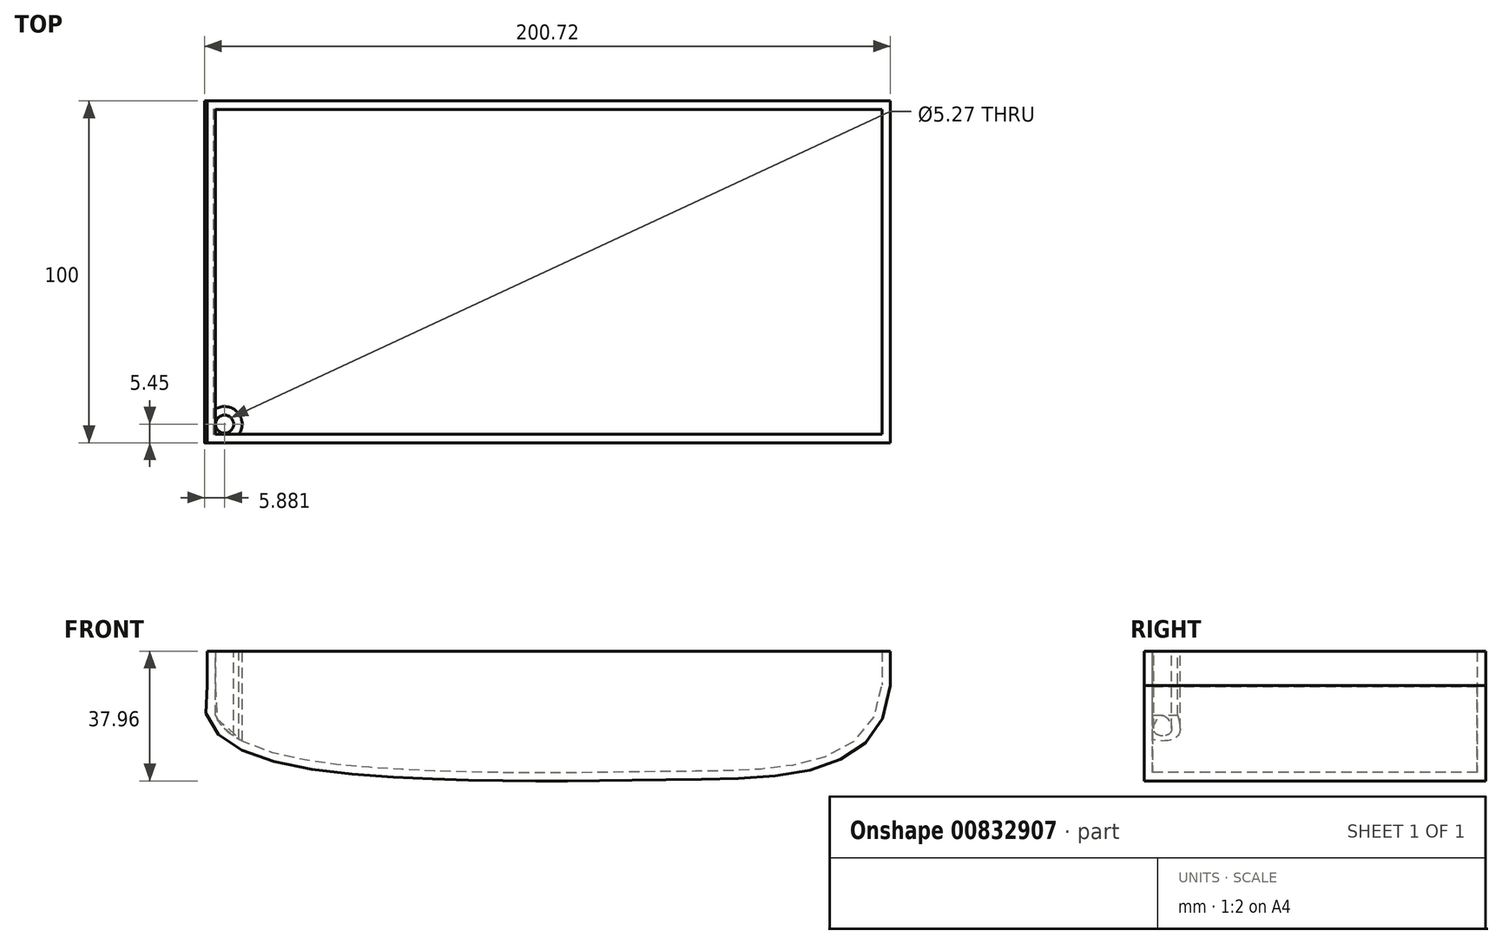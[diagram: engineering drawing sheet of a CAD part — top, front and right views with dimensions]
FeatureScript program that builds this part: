
annotation { "Feature Type Name" : "Feature", "Feature Type Description" : "" }
export const myFeature = defineFeature(function(context is Context, id is Id, definition is map)
    precondition{}
    {
        {
            var Q0;
            Q0=qCreatedBy(makeId("Front.planeOp"),FACE);
            var sketch = newSketch(context, id + "F0", { "sketchPlane" : qUnion([Q0])});
            skLineSegment(sketch, "E0.bottom", {"start": v(-100.49, -20.47) * mm, "end": v(99.51, -20.47) * mm});
            skLineSegment(sketch, "E0.left", {"start": v(-100.49, -20.47) * mm, "end": v(-100.49, -30.47) * mm});
            skLineSegment(sketch, "E0.right", {"start": v(99.51, -20.47) * mm, "end": v(99.51, -30.47) * mm});
            skFitSpline(sketch, "E1", {"points": [v(-100.49, -30.47) * mm, v(-42.17, -57.48) * mm, v(39.99, -57.98) * mm, v(99.51, -30.47) * mm], "startDerivative": vector(-59.48, -210.03) * mm, "endDerivative": vector(16.46, 256.73) * mm});
            skPoint(sketch, "E2.orphan", {"position": v(-100.49, -45.47) * mm});
            skPoint(sketch, "E3.orphan", {"position": v(99.51, -45.47) * mm});
            skSolve(sketch);
        }
        {
            var Q0;
            Q0=makeQuery(id+"F0.imprint","IMPRINT",FACE,{"disambiguationData":[TD([[makeQuery(id+"F0.imprint","IMPRINT",EDGE,{"derivedFrom":sQuery(id+"F0.wireOp",EDGE,"E0.bottom")}),-1.0]])]});
            extrude(context, id + "F1", {"entities" : qUnion([Q0]), "endBound" : BoundingType.SYMMETRIC, "depth" : 100 * mm, "offsetDistance" : 25 * mm});
        }
        {
            var Q0;
            Q0=makeQuery(id+"F1.opExtrude","SWEPT_FACE",FACE,{"disambiguationData":[OSD([sQuery(id+"F0.wireOp",EDGE,"E0.bottom")])]});
            shell(context, id + "F2", {"entities" : qUnion([Q0]), "thickness" : 2.5 * mm});
        }
        {
            var Q0;
            Q0=makeQuery(id+"F1.opExtrude","SWEPT_FACE",FACE,{"disambiguationData":[OSD([sQuery(id+"F0.wireOp",EDGE,"E0.bottom")])]});
            var sketch = newSketch(context, id + "F3", { "sketchPlane" : qUnion([Q0])});
            skCircle(sketch, "E4", {"center": v(-95.33, -44.55) * mm, "radius": 5.14 * mm});
            skCircle(sketch, "E5", {"center": v(-95.33, -44.55) * mm, "radius": 2.64 * mm});
            skSolve(sketch);
        }
        {
            var Q0;
            {var subQ0=sQuery(id+"F0.wireOp",EDGE,"E0.bottom");var subQ1=makeQuery(id+"F2.opShell","OFFSET_EDGE",EDGE,{"disambiguationData":[OSD([subQ0]),TDD([makeQuery(id+"F1.opExtrude","CAP_EDGE",EDGE,{"disambiguationData":[OSD([subQ0])],"isStart":false})])]});var subQ7=sQuery(id+"F3.wireOp",EDGE,"E4");var subQ8=makeQuery(id+"F3.imprint","INTERSECT",VERTEX,{"derivedFrom":[subQ1,subQ7]});Q0=makeQuery(id+"F3.imprint","IMPRINT",FACE,{"disambiguationData":[TD([[makeQuery(id+"F3.imprint","IMPRINT",EDGE,{"disambiguationData":[TD([[subQ8,-1.0]])],"derivedFrom":subQ7}),1.0]])]});}
            extrude(context, id + "F4", {"entities" : qUnion([Q0]), "endBound" : BoundingType.UP_TO_NEXT, "oppositeDirection" : true, "depth" : 25 * mm, "offsetDistance" : 25 * mm});
        }
    });
